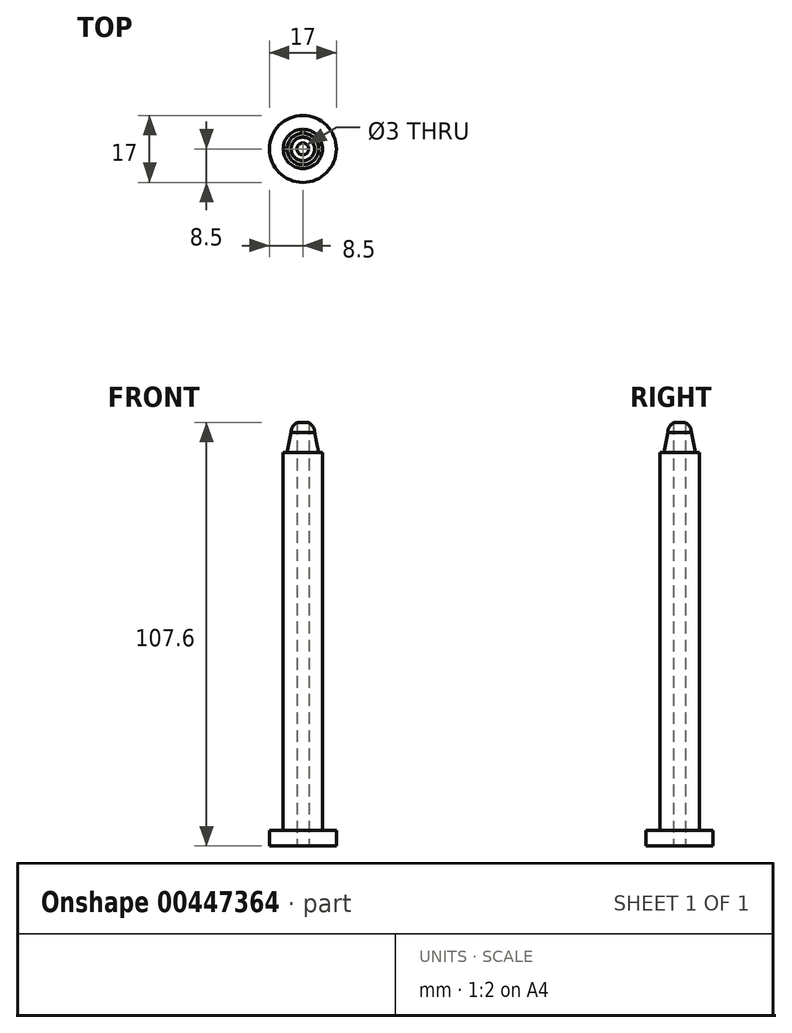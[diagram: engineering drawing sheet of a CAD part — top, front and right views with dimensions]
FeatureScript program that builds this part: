
annotation { "Feature Type Name" : "Feature", "Feature Type Description" : "" }
export const myFeature = defineFeature(function(context is Context, id is Id, definition is map)
    precondition{}
    {
        {
            var Q0;
            Q0=qCreatedBy(makeId("Top.planeOp"),FACE);
            var sketch = newSketch(context, id + "F0", { "sketchPlane" : qUnion([Q0])});
            skCircle(sketch, "E0", {"center": v(0, 0) * mm, "radius": 8.5 * mm});
            skSolve(sketch);
        }
        {
            var Q0;
            Q0=qSketchRegion(id+"F0",true);
            extrude(context, id + "F1", {"entities" : qUnion([Q0]), "depth" : 4 * mm});
        }
        {
            var Q0;
            Q0=qCreatedBy(makeId("Top.planeOp"),FACE);
            var sketch = newSketch(context, id + "F2", { "sketchPlane" : qUnion([Q0])});
            skCircle(sketch, "E1", {"center": v(0, 0) * mm, "radius": 5 * mm});
            skSolve(sketch);
        }
        {
            var Q0;
            Q0=qSketchRegion(id+"F2",true);
            extrude(context, id + "F3", {"entities" : qUnion([Q0]), "operationType" : NewBodyOperationType.ADD, "depth" : 100 * mm});
        }
        {
            var Q0;
            Q0=qCreatedBy(makeId("Right.planeOp"),FACE);
            var sketch = newSketch(context, id + "F4", { "sketchPlane" : qUnion([Q0])});
            skLineSegment(sketch, "E2", {"start": v(0, 105) * mm, "end": v(0, 100) * mm});
            skLineSegment(sketch, "E3", {"start": v(0, 100) * mm, "end": v(4, 100) * mm});
            skLineSegment(sketch, "E4", {"start": v(4, 100) * mm, "end": v(3, 105) * mm});
            skLineSegment(sketch, "E5", {"start": v(3, 105) * mm, "end": v(0, 105) * mm});
            skSolve(sketch);
        }
        {
            var Q0;
            Q0=makeQuery(id+"F4.imprint","IMPRINT",FACE,{"disambiguationData":[TD([[makeQuery(id+"F4.imprint","IMPRINT",EDGE,{"derivedFrom":sQuery(id+"F4.wireOp",EDGE,"E2")}),1.0]])]});
            var Q1;
            Q1=sQuery(id+"F4.wireOp",EDGE,"E2");
            revolve(context, id + "F5", {"operationType" : NewBodyOperationType.ADD, "entities" : qUnion([Q0]), "axis" : qUnion([Q1]), "revolveType" : RevolveType.FULL});
        }
        {
            var Q0;
            Q0=qCreatedBy(makeId("Right.planeOp"),FACE);
            var sketch = newSketch(context, id + "F6", { "sketchPlane" : qUnion([Q0])});
            skLineSegment(sketch, "E6", {"start": v(0, 108) * mm, "end": v(0, 105) * mm});
            skLineSegment(sketch, "E7", {"start": v(0, 105) * mm, "end": v(3, 105) * mm});
            skArc(sketch, "E8", {"start": v(3, 105) * mm, "mid": v(2.12, 107.12) * mm, "end": v(0, 108) * mm});
            skSolve(sketch);
        }
        {
            var Q0;
            Q0=makeQuery(id+"F6.imprint","IMPRINT",FACE,{"disambiguationData":[TD([[makeQuery(id+"F6.imprint","IMPRINT",EDGE,{"derivedFrom":sQuery(id+"F6.wireOp",EDGE,"E6")}),1.0]])]});
            var Q1;
            Q1=sQuery(id+"F6.wireOp",EDGE,"E6");
            revolve(context, id + "F7", {"operationType" : NewBodyOperationType.ADD, "entities" : qUnion([Q0]), "axis" : qUnion([Q1]), "revolveType" : RevolveType.FULL});
        }
        {
            var Q0;
            Q0=makeQuery(id+"F1.opExtrude","CAP_FACE",FACE,{"disambiguationData":[OSD([sQuery(id+"F0.wireOp",EDGE,"E0")])],"isStart":true});
            var sketch = newSketch(context, id + "F8", { "sketchPlane" : qUnion([Q0])});
            skCircle(sketch, "E9", {"center": v(0, 0) * mm, "radius": 1.5 * mm});
            skSolve(sketch);
        }
        {
            var Q0;
            Q0 = qSketchRegion(id + "F8", true);
            extrude(context, id + "F9", {"entities" : qUnion([Q0]), "operationType" : NewBodyOperationType.REMOVE, "oppositeDirection" : true, "depth" : 123.9 * mm});
        }
    });
